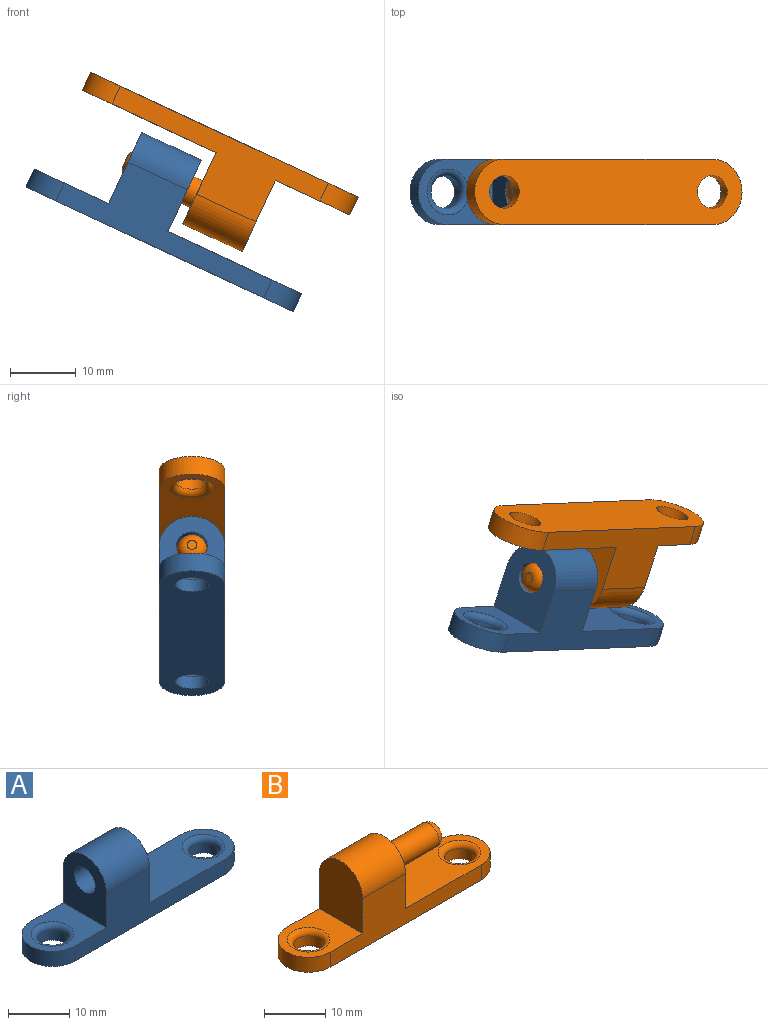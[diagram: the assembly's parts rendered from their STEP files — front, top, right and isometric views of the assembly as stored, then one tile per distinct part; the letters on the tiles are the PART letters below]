
ASSEMBLY  parts=2 mates=1
PART A: 15 faces, bbox 45x10x15 mm
  f0: plane 12.5x10mm, normal (0,0,1), area 75.8mm2, adj f1,f2,f5,f10,f12
  f1: cylinder r=5mm len=10mm, axis (0,0,-1), area 47.1mm2, adj f0,f2,f5,f8
  f2: plane 35x10mm, normal (0,-1,0), area 175mm2, adj f0,f1,f3,f7,f8,f9,f10,f11
  f3: cylinder r=5mm len=10mm, axis (0,0,-1), area 47.1mm2, adj f2,f5,f7,f8
  f4: cylinder r=2.5mm len=5mm, axis (0,0,-1), area 31.4mm2, adj f8,f12
  f5: plane 35x10mm, normal (0,1,0), area 175mm2, adj f0,f1,f3,f7,f8,f9,f10,f11
  f6: cylinder r=2.5mm len=5mm, axis (0,0,-1), area 31.4mm2, adj f8,f13
  f7: plane 22.5x10mm, normal (0,0,1), area 175.8mm2, adj f2,f3,f5,f9,f13
  f8: plane 45x10mm, normal (0,0,-1), area 389.3mm2, adj f1,f2,f3,f4,f5,f6
  f9: plane 12x10mm, normal (1,0,0), area 91.2mm2, adj f2,f5,f7,f11,f14
  f10: plane 12x10mm, normal (-1,0,0), area 91.2mm2, adj f0,f2,f5,f11,f14
  f11: cylinder r=5mm len=10mm, axis (-1,0,0), area 157.1mm2, adj f2,f5,f9,f10
  f12: torus R=3.5mm, axis (0,0,1), area 28.3mm2, adj f0,f4
  f13: torus R=3.5mm, axis (0,0,1), area 28.3mm2, adj f6,f7
  f14: cylinder r=2.4mm len=10mm, axis (1,0,0), area 150.8mm2, adj f9,f10
PART B: 17 faces, bbox 45x10x15 mm
  f0: plane 12.5x10mm, normal (0,0,1), area 75.8mm2, adj f1,f2,f5,f10,f12
  f1: cylinder r=5mm len=10mm, axis (0,0,-1), area 47.1mm2, adj f0,f2,f5,f8
  f2: plane 35x10mm, normal (0,-1,0), area 175mm2, adj f0,f1,f3,f7,f8,f9,f10,f11
  f3: cylinder r=5mm len=10mm, axis (0,0,-1), area 47.1mm2, adj f2,f5,f7,f8
  f4: cylinder r=2.5mm len=5mm, axis (0,0,-1), area 31.4mm2, adj f8,f12
  f5: plane 35x10mm, normal (0,1,0), area 175mm2, adj f0,f1,f3,f7,f8,f9,f10,f11
  f6: cylinder r=2.5mm len=5mm, axis (0,0,-1), area 31.4mm2, adj f8,f13
  f7: plane 22.5x10mm, normal (0,0,1), area 175.8mm2, adj f2,f3,f5,f9,f13
  f8: plane 45x10mm, normal (0,0,-1), area 389.3mm2, adj f1,f2,f3,f4,f5,f6
  f9: plane 12x10mm, normal (1,0,0), area 93.4mm2, adj f2,f5,f7,f11,f14
  f10: plane 12x10mm, normal (-1,0,0), area 109.3mm2, adj f0,f2,f5,f11
  f11: cylinder r=5mm len=10mm, axis (-1,0,0), area 157.1mm2, adj f2,f5,f9,f10
  f12: torus R=3.5mm, axis (0,0,1), area 28.3mm2, adj f0,f4
  f13: torus R=3.5mm, axis (0,0,1), area 28.3mm2, adj f6,f7
  f14: cylinder r=2.25mm len=10.5mm, axis (-1,0,0), area 148.4mm2, adj f9,f16
  f15: plane 1.5x1.5mm, normal (1,0,0), area 1.8mm2, adj f16
  f16: torus R=0.75mm, axis (1,0,0), area 25.2mm2, adj f14,f15
PLACE A rot(axis=(0,1,0),25deg) t=(0.19,0,0.57)mm
PLACE B rot(axis=(0,-1,0),155deg) t=(-35.26,0,39.16)mm
MATE revolute B.f11 <-> A.f11  axis (-0.91,0,0.42) through (-49.97,0,34.99)mm
